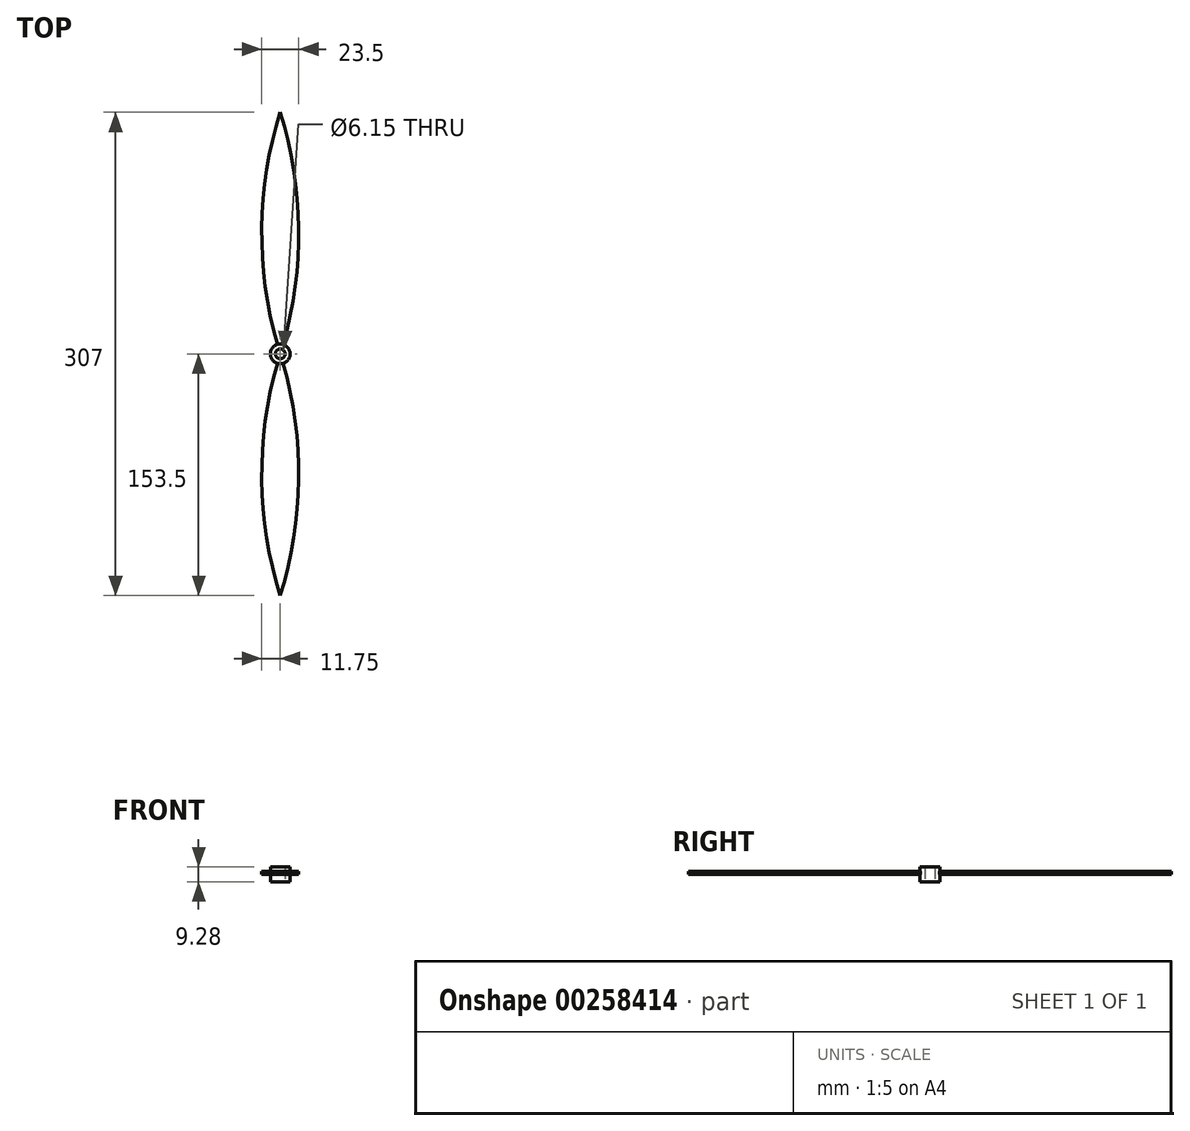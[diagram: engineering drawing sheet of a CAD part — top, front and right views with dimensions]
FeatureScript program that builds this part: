
annotation { "Feature Type Name" : "Feature", "Feature Type Description" : "" }
export const myFeature = defineFeature(function(context is Context, id is Id, definition is map)
    precondition{}
    {
        {
            var Q0;
            Q0=qCreatedBy(makeId("Top.planeOp"),FACE);
            var sketch = newSketch(context, id + "F0", { "sketchPlane" : qUnion([Q0])});
            skLineSegment(sketch, "E0", {"start": v(0, 153.5) * mm, "end": v(0, 0) * mm, "construction": true});
            skLineSegment(sketch, "E1.MirrorCS", {"start": v(0, -153.5) * mm, "end": v(0, 0) * mm, "construction": true});
            skArc(sketch, "E2", {"start": v(1.8, 5.99) * mm, "mid": v(11.73, 79.87) * mm, "end": v(0, 153.5) * mm});
            skArc(sketch, "E3.MirrorCS", {"start": v(-1.8, 5.99) * mm, "mid": v(-11.73, 79.87) * mm, "end": v(0, 153.5) * mm});
            skArc(sketch, "E4.MirrorCS", {"start": v(-1.8, -5.99) * mm, "mid": v(-11.73, -79.87) * mm, "end": v(0, -153.5) * mm});
            skArc(sketch, "E5.MirrorCS", {"start": v(1.8, -5.99) * mm, "mid": v(11.73, -79.87) * mm, "end": v(0, -153.5) * mm});
            skCircle(sketch, "E6", {"center": v(0, 0) * mm, "radius": 3.1 * mm});
            skCircle(sketch, "E7", {"center": v(0, 0) * mm, "radius": 6.25 * mm});
            skSolve(sketch);
        }
        {
            var Q0;
            {var subQ0=sQuery(id+"F0.wireOp",EDGE,"E2");Q0=makeQuery(id+"F0.imprint","IMPRINT",FACE,{"disambiguationData":[TD([[makeQuery(id+"F0.imprint","IMPRINT",EDGE,{"derivedFrom":subQ0}),1.0]])]});}
            var Q1;
            {var subQ0=sQuery(id+"F0.wireOp",EDGE,"E4.MirrorCS");Q1=makeQuery(id+"F0.imprint","IMPRINT",FACE,{"disambiguationData":[TD([[makeQuery(id+"F0.imprint","IMPRINT",EDGE,{"derivedFrom":subQ0}),1.0]])]});}
            extrude(context, id + "F1", {"entities" : qUnion([Q0, Q1]), "depth" : 2 * mm});
        }
        {
            var Q0;
            Q0=qCreatedBy(makeId("Top.planeOp"),FACE);
            var sketch = newSketch(context, id + "F2", { "sketchPlane" : qUnion([Q0])});
            skCircle(sketch, "E8", {"center": v(0, 0) * mm, "radius": 6.25 * mm});
            skCircle(sketch, "E9", {"center": v(0, 0) * mm, "radius": 3.08 * mm});
            skSolve(sketch);
        }
        {
            var Q0;
            Q0=makeQuery(id+"F2.imprint","IMPRINT",FACE,{"disambiguationData":[TD([[makeQuery(id+"F2.imprint","IMPRINT",EDGE,{"derivedFrom":sQuery(id+"F2.wireOp",EDGE,"E8")}),1.0]])]});
            extrude(context, id + "F3", {"entities" : qUnion([Q0]), "depth" : 9.28 * mm, "symmetric" : true});
        }
    });
